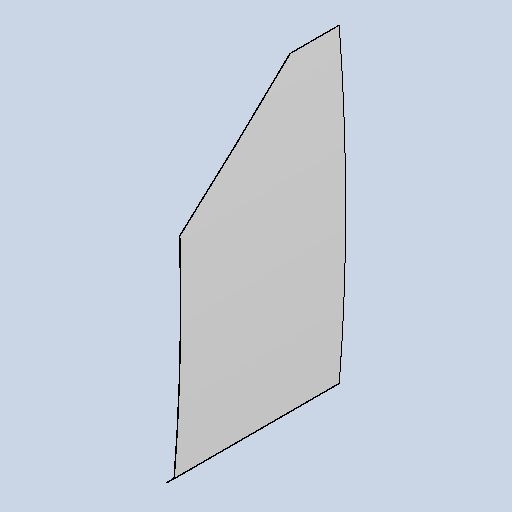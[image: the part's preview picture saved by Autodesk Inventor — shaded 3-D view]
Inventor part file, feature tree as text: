
AUTODESK INVENTOR PART (.ipt)
format: ipt  version: 2025 (Build 290162010, 162A)  size: 329,728 bytes
history: native  units: mm
features: other x4, sheet_metal_op x3, sketch x3, extrude x1
ambient origin geometry x8: Origin, YZ Plane, XZ Plane, XY Plane, X Axis, Y Axis, Z Axis, Center Point
bodies: Body1 (feature_tree)
feature tree (11):
  sheet_metal_op  "Contour Flange2"
  extrude  "Extrusion3"  Depth=3.0mm
  other  "Mark5"
  other  "A-Side Definition"
  sketch  "Sketch1"  dims[d36=3.0mm d37=3.0mm]
  other  "Plate2"
  sheet_metal_op  "Bend2"
  sheet_metal_op  "Corner2"
  sketch  "Sketch6"  dims[d38=1.5mm]
  sketch  "Sketch7"  dims[d39=6.0mm d40=3.0mm d41=980.0mm d42=3.0mm d43=3.0mm d44=12.0mm d45=3.0mm d46=3.0mm d65=6.0mm d78=3.0mm d80=3.0mm d154=5.0mm d155=63.0mm d156=11050.0mm d157=23.736478mm d159=5.0mm d160=6.981317mm d161=291.0mm d162=10.0mm d163=0.0mm d164=0.0mm d165=1843.0mm]
  other  "Definition1"
